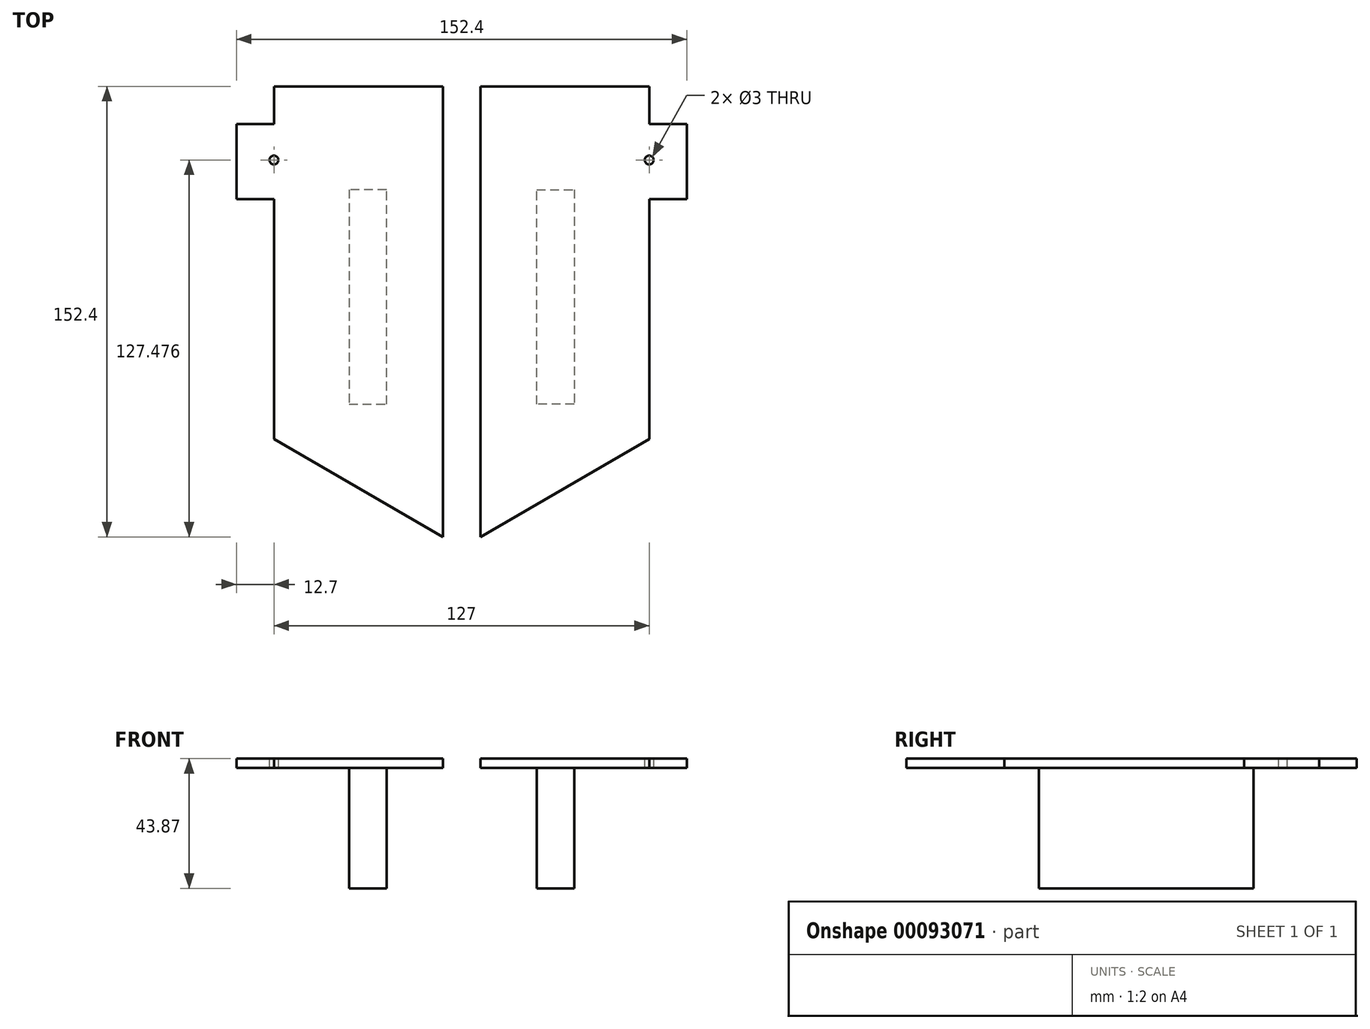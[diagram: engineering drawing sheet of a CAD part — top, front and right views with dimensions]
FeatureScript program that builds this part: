
annotation { "Feature Type Name" : "Feature", "Feature Type Description" : "" }
export const myFeature = defineFeature(function(context is Context, id is Id, definition is map)
    precondition{}
    {
        {
            var Q0;
            Q0=qCreatedBy(makeId("Top.planeOp"),FACE);
            var sketch = newSketch(context, id + "F0", { "sketchPlane" : qUnion([Q0])});
            skLineSegment(sketch, "E0.bottom", {"start": v(-82.55, 213.29) * mm, "end": v(82.55, 213.29) * mm, "construction": true});
            skLineSegment(sketch, "E0.top", {"start": v(-82.55, -66.11) * mm, "end": v(82.55, -66.11) * mm, "construction": true});
            skLineSegment(sketch, "E0.left", {"start": v(-82.55, 213.29) * mm, "end": v(-82.55, -66.11) * mm, "construction": true});
            skLineSegment(sketch, "E0.right", {"start": v(82.55, 213.29) * mm, "end": v(82.55, -66.11) * mm, "construction": true});
            skPoint(sketch, "E1.right.end.orphan", {"position": v(82.55, -193.11) * mm});
            skLineSegment(sketch, "E2", {"start": v(0, 213.29) * mm, "end": v(-25.4, 213.29) * mm});
            skLineSegment(sketch, "E3", {"start": v(0, 213.29) * mm, "end": v(25.4, 213.29) * mm});
            skLineSegment(sketch, "E4", {"start": v(-25.4, 213.29) * mm, "end": v(-25.4, 191.06) * mm});
            skLineSegment(sketch, "E5", {"start": v(25.4, 213.29) * mm, "end": v(25.4, 191.06) * mm});
            skLineSegment(sketch, "E6", {"start": v(-25.4, 191.06) * mm, "end": v(-50.8, 191.06) * mm});
            skLineSegment(sketch, "E7", {"start": v(25.4, 191.06) * mm, "end": v(50.8, 191.06) * mm});
            skLineSegment(sketch, "E8", {"start": v(-50.8, 191.06) * mm, "end": v(-50.8, -66.11) * mm});
            skLineSegment(sketch, "E9", {"start": v(50.8, 191.06) * mm, "end": v(50.8, -66.11) * mm});
            skLineSegment(sketch, "E10", {"start": v(-50.8, -66.11) * mm, "end": v(50.8, -66.11) * mm});
            skLineSegment(sketch, "E11", {"start": v(-25.4, 178.36) * mm, "end": v(25.4, 178.36) * mm});
            skLineSegment(sketch, "E12", {"start": v(-25.4, 178.36) * mm, "end": v(-25.4, 105.77) * mm});
            skLineSegment(sketch, "E13", {"start": v(-25.4, 105.77) * mm, "end": v(25.4, 105.77) * mm});
            skLineSegment(sketch, "E14", {"start": v(25.4, 105.77) * mm, "end": v(25.4, 178.36) * mm});
            skSolve(sketch);
        }
        {
            var Q0;
            Q0=qCreatedBy(makeId("Right.planeOp"),FACE);
            cPlane(context, id + "F1", {"entities" : qUnion([Q0]), "cplaneType" : CPlaneType.OFFSET, "offset" : 76.2 * mm, "width" : 152.4 * mm, "height" : 152.4 * mm});
        }
        {
            var Q0;
            Q0=qCreatedBy(id+"F1.planeOp",FACE);
            var sketch = newSketch(context, id + "F2", { "sketchPlane" : qUnion([Q0])});
            skPoint(sketch, "E15.0", {"position": v(213.29, 0) * mm});
            skPoint(sketch, "E16.0", {"position": v(-66.11, 0) * mm});
            skLineSegment(sketch, "E17", {"start": v(213.29, 3.17) * mm, "end": v(213.29, 0) * mm});
            skLineSegment(sketch, "E18", {"start": v(213.29, 3.17) * mm, "end": v(60.89, 3.17) * mm});
            skLineSegment(sketch, "E19", {"start": v(60.89, 3.17) * mm, "end": v(60.89, 0) * mm});
            skLineSegment(sketch, "E20", {"start": v(60.89, 0) * mm, "end": v(213.29, 0) * mm});
            skSolve(sketch);
        }
        {
            var Q0;
            Q0=makeQuery(id+"F2.imprint","IMPRINT",FACE,{"disambiguationData":[TD([[makeQuery(id+"F2.imprint","IMPRINT",EDGE,{"derivedFrom":sQuery(id+"F2.wireOp",EDGE,"E17")}),-1.0]])]});
            extrude(context, id + "F3", {"entities" : qUnion([Q0]), "oppositeDirection" : true, "depth" : 69.85 * mm});
        }
        {
            var Q0;
            Q0=makeQuery(id+"F3.opExtrude","SWEPT_FACE",FACE,{"disambiguationData":[OSD([sQuery(id+"F2.wireOp",EDGE,"E18")])]});
            var sketch = newSketch(context, id + "F4", { "sketchPlane" : qUnion([Q0])});
            skPoint(sketch, "E21.0", {"position": v(76.2, 213.29) * mm});
            skPoint(sketch, "E22.0", {"position": v(76.2, 60.89) * mm});
            skLineSegment(sketch, "E23", {"start": v(63.5, 213.29) * mm, "end": v(63.5, 60.89) * mm});
            skLineSegment(sketch, "E24", {"start": v(63.5, 200.59) * mm, "end": v(76.2, 200.59) * mm});
            skLineSegment(sketch, "E25", {"start": v(63.5, 175.19) * mm, "end": v(76.2, 175.19) * mm});
            skSolve(sketch);
        }
        {
            var Q0;
            {var subQ4=sQuery(id+"F4.wireOp",EDGE,"E25");Q0=makeQuery(id+"F4.imprint","IMPRINT",FACE,{"disambiguationData":[TD([[makeQuery(id+"F4.imprint","IMPRINT",EDGE,{"derivedFrom":subQ4}),-1.0]])]});}
            var Q1;
            {var subQ4=sQuery(id+"F4.wireOp",EDGE,"E24");Q1=makeQuery(id+"F4.imprint","IMPRINT",FACE,{"disambiguationData":[TD([[makeQuery(id+"F4.imprint","IMPRINT",EDGE,{"derivedFrom":subQ4}),1.0]])]});}
            extrude(context, id + "F5", {"entities" : qUnion([Q0, Q1]), "operationType" : NewBodyOperationType.REMOVE, "oppositeDirection" : true, "depth" : 254 * mm});
        }
        {
            var Q0;
            Q0=makeQuery(id+"F3.opExtrude","SWEPT_FACE",FACE,{"disambiguationData":[OSD([sQuery(id+"F2.wireOp",EDGE,"E19")])]});
            var sketch = newSketch(context, id + "F6", { "sketchPlane" : qUnion([Q0])});
            skPoint(sketch, "E26.0", {"position": v(6.35, 3.17) * mm});
            skPoint(sketch, "E27.0", {"position": v(6.35, 0) * mm});
            skLineSegment(sketch, "E28", {"start": v(6.35, 1.59) * mm, "end": v(6.35, 25.4) * mm});
            skLineSegment(sketch, "E29", {"start": v(6.35, 1.59) * mm, "end": v(6.35, -22.23) * mm});
            skLineSegment(sketch, "E30.bottom", {"start": v(6.35, 25.4) * mm, "end": v(57.15, 25.4) * mm});
            skLineSegment(sketch, "E30.top", {"start": v(6.35, -22.23) * mm, "end": v(57.15, -22.23) * mm});
            skLineSegment(sketch, "E30.left", {"start": v(6.35, 25.4) * mm, "end": v(6.35, -22.23) * mm});
            skLineSegment(sketch, "E30.right", {"start": v(57.15, 25.4) * mm, "end": v(57.15, -22.23) * mm});
            skSolve(sketch);
        }
        {
            var Q0;
            {var subQ0=sQuery(id+"F6.wireOp",EDGE,"E30.bottom");Q0=makeQuery(id+"F6.imprint","IMPRINT",FACE,{"disambiguationData":[TD([[makeQuery(id+"F6.imprint","IMPRINT",EDGE,{"derivedFrom":subQ0}),-1.0]])]});}
            extrude(context, id + "F7", {"entities" : qUnion([Q0]), "operationType" : NewBodyOperationType.REMOVE, "oppositeDirection" : true, "depth" : 254 * mm});
        }
        {
            var Q0;
            Q0=makeQuery(id+"F3.opExtrude","SWEPT_FACE",FACE,{"disambiguationData":[OSD([sQuery(id+"F2.wireOp",EDGE,"E18")])]});
            var sketch = newSketch(context, id + "F8", { "sketchPlane" : qUnion([Q0])});
            skLineSegment(sketch, "E31", {"start": v(6.35, 60.89) * mm, "end": v(63.5, 94.02) * mm});
            skLineSegment(sketch, "E32", {"start": v(63.5, 94.02) * mm, "end": v(63.5, 60.89) * mm});
            skLineSegment(sketch, "E33", {"start": v(63.5, 60.89) * mm, "end": v(6.35, 60.89) * mm});
            skSolve(sketch);
        }
        {
            var Q0;
            Q0=makeQuery(id+"F8.imprint","IMPRINT",FACE,{"disambiguationData":[TD([[makeQuery(id+"F8.imprint","IMPRINT",EDGE,{"derivedFrom":sQuery(id+"F8.wireOp",EDGE,"E31")}),-1.0]])]});
            extrude(context, id + "F9", {"entities" : qUnion([Q0]), "operationType" : NewBodyOperationType.REMOVE, "oppositeDirection" : true, "depth" : 254 * mm});
        }
        {
            var Q0;
            Q0=makeQuery(id+"F3.opExtrude","SWEPT_FACE",FACE,{"disambiguationData":[OSD([sQuery(id+"F2.wireOp",EDGE,"E18")])]});
            var sketch = newSketch(context, id + "F10", { "sketchPlane" : qUnion([Q0])});
            skCircle(sketch, "E34", {"center": v(63.5, 188.37) * mm, "radius": 1.5 * mm});
            skPoint(sketch, "E35.0", {"position": v(50.8, 191.06) * mm});
            skPoint(sketch, "E36.0", {"position": v(82.55, 213.29) * mm});
            skSolve(sketch);
        }
        {
            var Q0;
            Q0=makeQuery(id+"F10.imprint","IMPRINT",FACE,{"disambiguationData":[TD([[makeQuery(id+"F10.imprint","IMPRINT",EDGE,{"derivedFrom":sQuery(id+"F10.wireOp",EDGE,"E34")}),1.0]])]});
            extrude(context, id + "F11", {"entities" : qUnion([Q0]), "operationType" : NewBodyOperationType.REMOVE, "oppositeDirection" : true, "depth" : 254 * mm});
        }
        {
            var Q0;
            Q0=makeQuery(id+"F3.opExtrude","SWEPT_FACE",FACE,{"disambiguationData":[OSD([sQuery(id+"F2.wireOp",EDGE,"E20")])]});
            var sketch = newSketch(context, id + "F12", { "sketchPlane" : qUnion([Q0])});
            skPoint(sketch, "E37.0", {"position": v(25.4, -178.36) * mm});
            skPoint(sketch, "E38.0", {"position": v(25.4, -105.77) * mm});
            skLineSegment(sketch, "E39", {"start": v(25.4, -178.36) * mm, "end": v(63.5, -178.36) * mm});
            skLineSegment(sketch, "E40", {"start": v(63.5, -178.36) * mm, "end": v(63.5, -105.77) * mm});
            skLineSegment(sketch, "E41", {"start": v(63.5, -105.77) * mm, "end": v(25.4, -105.77) * mm});
            skLineSegment(sketch, "E42", {"start": v(25.4, -105.77) * mm, "end": v(25.4, -178.36) * mm});
            skLineSegment(sketch, "E43", {"start": v(38.1, -178.36) * mm, "end": v(38.1, -105.77) * mm});
            skSolve(sketch);
        }
        {
            var Q0;
            Q0=qCreatedBy(makeId("Top.planeOp"),FACE);
            var sketch = newSketch(context, id + "F13", { "sketchPlane" : qUnion([Q0])});
            skPoint(sketch, "E44.0", {"position": v(38.1, 178.36) * mm});
            skLineSegment(sketch, "E45.0", {"start": v(38.1, 178.36) * mm, "end": v(38.1, 105.77) * mm});
            skLineSegment(sketch, "E46.0", {"start": v(25.4, 105.77) * mm, "end": v(25.4, 178.36) * mm});
            skLineSegment(sketch, "E47.0", {"start": v(25.4, 178.36) * mm, "end": v(38.1, 178.36) * mm});
            skPoint(sketch, "E48.orphan", {"position": v(63.5, 178.36) * mm});
            skLineSegment(sketch, "E49.0", {"start": v(38.1, 105.77) * mm, "end": v(25.4, 105.77) * mm});
            skPoint(sketch, "E50.orphan", {"position": v(63.5, 105.77) * mm});
            skSolve(sketch);
        }
        {
            var Q0;
            Q0=qSketchRegion(id+"F13",true);
            extrude(context, id + "F14", {"entities" : qUnion([Q0]), "operationType" : NewBodyOperationType.ADD, "oppositeDirection" : true, "depth" : 40.7 * mm});
        }
        {
            var Q0;
            Q0=makeQuery(id+"F3.opExtrude","SWEPT_BODY",BODY,{"disambiguationData":[OSD([sQuery(id+"F2.wireOp",EDGE,"E17"),sQuery(id+"F2.wireOp",EDGE,"E18"),sQuery(id+"F2.wireOp",EDGE,"E19"),sQuery(id+"F2.wireOp",EDGE,"E20")])]});
            var Q1;
            Q1=qCreatedBy(makeId("Right.planeOp"),FACE);
            mirror(context, id + "F15", {"entities" : qUnion([Q0]), "mirrorPlane" : qUnion([Q1])});
        }
    });
